# Revit family: Table-Teknion-NVBT-Vignette_Coffee_Table-R2020
name_source: partatom
category: Furniture
units: mm (PartAtom-declared; Revit-internal decimal feet)

## family parameters
Always vertical = No
Cut with Voids When Loaded = No
OmniClass Number = 23.40.20.00
OmniClass Title = General Furniture and Specialties
Room Calculation Point = No
Shared = No
Work Plane-Based = No

## types (2) — shared parameters
Assembly Code = E2020200
Default Elevation = 0' - 0"
Height = 1' - 5 1/2"
Keynote = 125000
Manufacturer = Teknion
Product Documentation Link = http://www.teknion.com
Product Name = Vignette
Product Page URL = http://www.teknion.com
Table Base = Paint - Teknion - C - Chrome
URL = www.teknion.com

## per-type parameters (varying)
| type | Circular Top | Description | Model | Square Top | Table Top |
| Vignette Square Table | No | Square Coffee Table | NVBTS | Yes | Veneer-Teknion-5S-Flintwood-Silverwash |
| Vignette Round Table | Yes | Round Coffee Table | NVBTR | No | Veneer-Teknion-UK-Natural_Veneer_V2-Medium_Dark_Cherry |

## geometry (parser evidence)
native form markers: Blend x2, Sweep x9
no freeform markers — native parametric forms only
